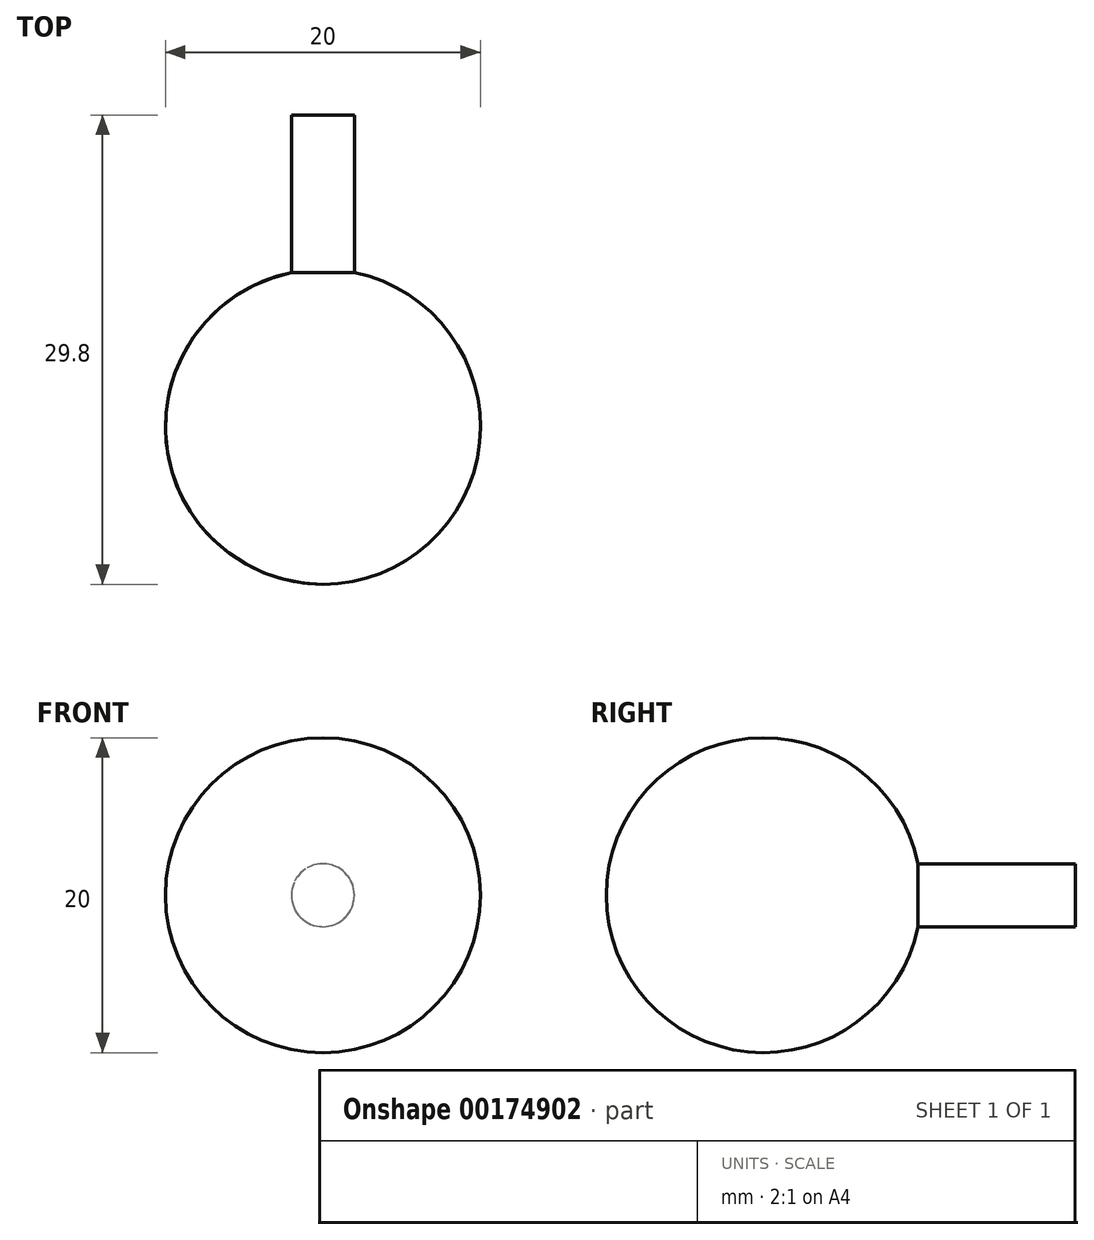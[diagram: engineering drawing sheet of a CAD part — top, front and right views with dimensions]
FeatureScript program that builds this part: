
annotation { "Feature Type Name" : "Feature", "Feature Type Description" : "" }
export const myFeature = defineFeature(function(context is Context, id is Id, definition is map)
    precondition{}
    {
        {
            var Q0;
            Q0=qCreatedBy(makeId("Top.planeOp"),FACE);
            var sketch = newSketch(context, id + "F0", { "sketchPlane" : qUnion([Q0])});
            skArc(sketch, "E0", {"start": v(0, -10) * mm, "mid": v(9.95, -1) * mm, "end": v(2, 9.8) * mm});
            skLineSegment(sketch, "E1.bottom", {"start": v(0, 19.8) * mm, "end": v(2, 19.8) * mm});
            skLineSegment(sketch, "E1.left", {"start": v(0, 19.8) * mm, "end": v(0, 9.8) * mm});
            skLineSegment(sketch, "E1.right", {"start": v(2, 19.8) * mm, "end": v(2, 9.8) * mm});
            skLineSegment(sketch, "E2", {"start": v(0, 9.8) * mm, "end": v(0, -10) * mm});
            skSolve(sketch);
        }
        {
            var Q0;
            {var subQ4=sQuery(id+"F0.wireOp",EDGE,"E1.bottom");Q0=makeQuery(id+"F0.imprint","IMPRINT",FACE,{"disambiguationData":[TD([[makeQuery(id+"F0.imprint","IMPRINT",EDGE,{"derivedFrom":subQ4}),-1.0]])]});}
            var Q1;
            {var subQ2=sQuery(id+"F0.wireOp",EDGE,"E1.top");Q1=makeQuery(id+"F0.imprint","IMPRINT",FACE,{"disambiguationData":[TD([[makeQuery(id+"F0.imprint","IMPRINT",EDGE,{"derivedFrom":subQ2}),-1.0]])]});}
            var Q2;
            Q2=sQuery(id+"F0.wireOp",EDGE,"E2");
            revolve(context, id + "F1", {"entities" : qUnion([Q0, Q1]), "axis" : qUnion([Q2]), "revolveType" : RevolveType.FULL});
        }
    });
